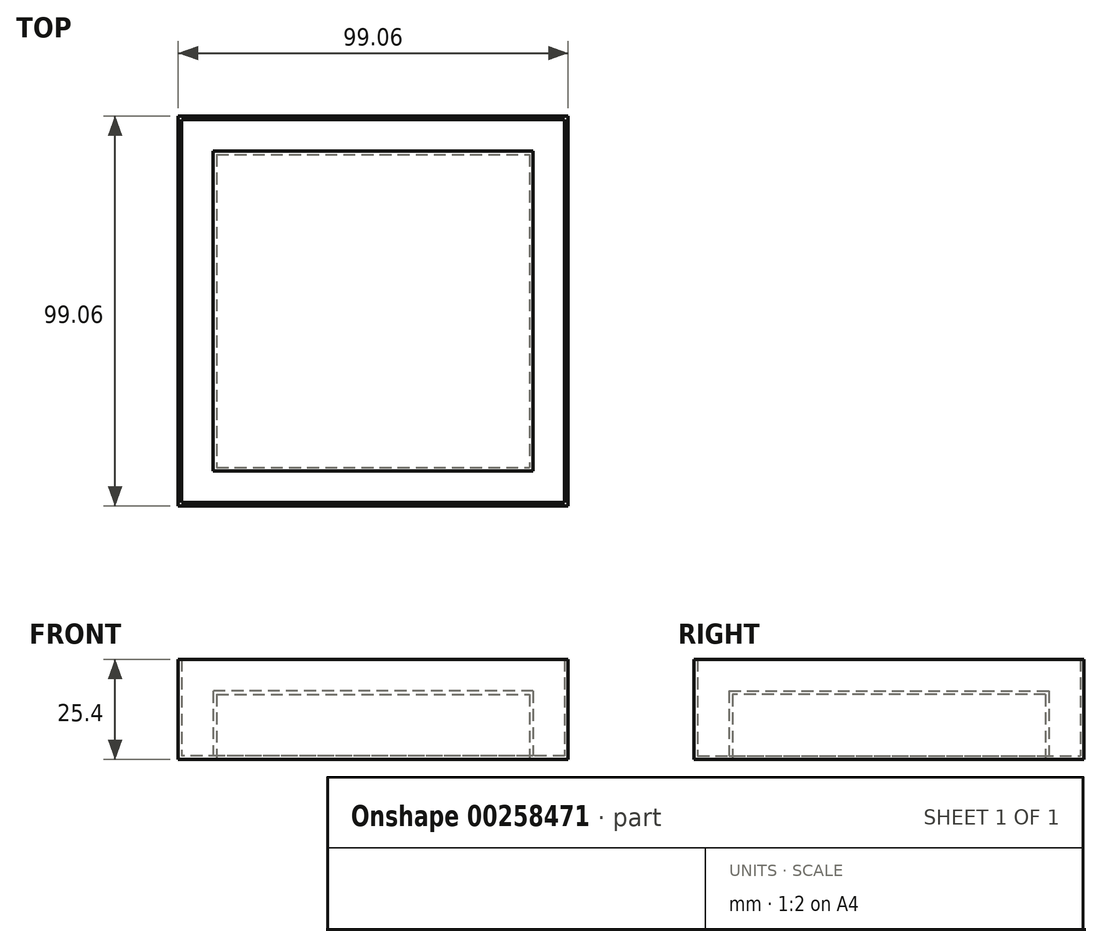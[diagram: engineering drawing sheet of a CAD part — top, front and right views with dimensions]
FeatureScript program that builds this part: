
annotation { "Feature Type Name" : "Feature", "Feature Type Description" : "" }
export const myFeature = defineFeature(function(context is Context, id is Id, definition is map)
    precondition{}
    {
        {
            var Q0;
            Q0=qCreatedBy(makeId("Top.planeOp"),FACE);
            var sketch = newSketch(context, id + "F0", { "sketchPlane" : qUnion([Q0])});
            skLineSegment(sketch, "E0.bottom", {"start": v(49.53, -49.53) * mm, "end": v(-49.53, -49.53) * mm});
            skLineSegment(sketch, "E0.top", {"start": v(49.53, 49.53) * mm, "end": v(-49.53, 49.53) * mm});
            skLineSegment(sketch, "E0.left", {"start": v(49.53, -49.53) * mm, "end": v(49.53, 49.53) * mm});
            skLineSegment(sketch, "E0.right", {"start": v(-49.53, -49.53) * mm, "end": v(-49.53, 49.53) * mm});
            skPoint(sketch, "E0.middle", {"position": v(0, 0) * mm});
            skSolve(sketch);
        }
        {
            var Q0;
            Q0=makeQuery(id+"F0.imprint","IMPRINT",FACE,{"disambiguationData":[TD([[makeQuery(id+"F0.imprint","IMPRINT",EDGE,{"derivedFrom":sQuery(id+"F0.wireOp",EDGE,"E0.bottom")}),-1.0]])]});
            extrude(context, id + "F1", {"entities" : qUnion([Q0]), "depth" : 25.4 * mm});
        }
        {
            var Q0;
            Q0=makeQuery(id+"F1.opExtrude","CAP_FACE",FACE,{"disambiguationData":[OSD([sQuery(id+"F0.wireOp",EDGE,"E0.bottom"),sQuery(id+"F0.wireOp",EDGE,"E0.top"),sQuery(id+"F0.wireOp",EDGE,"E0.left"),sQuery(id+"F0.wireOp",EDGE,"E0.right")])],"isStart":false});
            shell(context, id + "F2", {"entities" : qUnion([Q0]), "thickness" : 0.89 * mm});
        }
        {
            var Q0;
            Q0=makeQuery(id+"F2.opShell","OFFSET_FACE",FACE,{"disambiguationData":[OSD([sQuery(id+"F0.wireOp",EDGE,"E0.bottom"),sQuery(id+"F0.wireOp",EDGE,"E0.top"),sQuery(id+"F0.wireOp",EDGE,"E0.left"),sQuery(id+"F0.wireOp",EDGE,"E0.right")])]});
            var sketch = newSketch(context, id + "F3", { "sketchPlane" : qUnion([Q0])});
            skLineSegment(sketch, "E1.bottom", {"start": v(40.64, -40.64) * mm, "end": v(-40.64, -40.64) * mm});
            skLineSegment(sketch, "E1.top", {"start": v(40.64, 40.64) * mm, "end": v(-40.64, 40.64) * mm});
            skLineSegment(sketch, "E1.left", {"start": v(40.64, -40.64) * mm, "end": v(40.64, 40.64) * mm});
            skLineSegment(sketch, "E1.right", {"start": v(-40.64, -40.64) * mm, "end": v(-40.64, 40.64) * mm});
            skPoint(sketch, "E1.middle", {"position": v(0, 0) * mm});
            skSolve(sketch);
        }
        {
            var Q0;
            Q0=makeQuery(id+"F3.imprint","IMPRINT",FACE,{"disambiguationData":[TD([[makeQuery(id+"F3.imprint","IMPRINT",EDGE,{"derivedFrom":sQuery(id+"F3.wireOp",EDGE,"E1.bottom")}),-1.0]])]});
            extrude(context, id + "F4", {"entities" : qUnion([Q0]), "operationType" : NewBodyOperationType.ADD, "depth" : 16.5 * mm});
        }
        {
            var Q0;
            Q0=makeQuery(id+"F1.opExtrude","CAP_FACE",FACE,{"disambiguationData":[OSD([sQuery(id+"F0.wireOp",EDGE,"E0.bottom"),sQuery(id+"F0.wireOp",EDGE,"E0.top"),sQuery(id+"F0.wireOp",EDGE,"E0.left"),sQuery(id+"F0.wireOp",EDGE,"E0.right")])],"isStart":true});
            var sketch = newSketch(context, id + "F5", { "sketchPlane" : qUnion([Q0])});
            skLineSegment(sketch, "E2.bottom", {"start": v(-39.75, -39.75) * mm, "end": v(39.75, -39.75) * mm});
            skLineSegment(sketch, "E2.top", {"start": v(-39.75, 39.75) * mm, "end": v(39.75, 39.75) * mm});
            skLineSegment(sketch, "E2.left", {"start": v(-39.75, -39.75) * mm, "end": v(-39.75, 39.75) * mm});
            skLineSegment(sketch, "E2.right", {"start": v(39.75, -39.75) * mm, "end": v(39.75, 39.75) * mm});
            skPoint(sketch, "E2.middle", {"position": v(0, 0) * mm});
            skSolve(sketch);
        }
        {
            var Q0;
            Q0=makeQuery(id+"F5.imprint","IMPRINT",FACE,{"disambiguationData":[TD([[makeQuery(id+"F5.imprint","IMPRINT",EDGE,{"derivedFrom":sQuery(id+"F5.wireOp",EDGE,"E2.bottom")}),1.0]])]});
            extrude(context, id + "F6", {"entities" : qUnion([Q0]), "operationType" : NewBodyOperationType.REMOVE, "oppositeDirection" : true, "depth" : 16.5 * mm});
        }
    });
